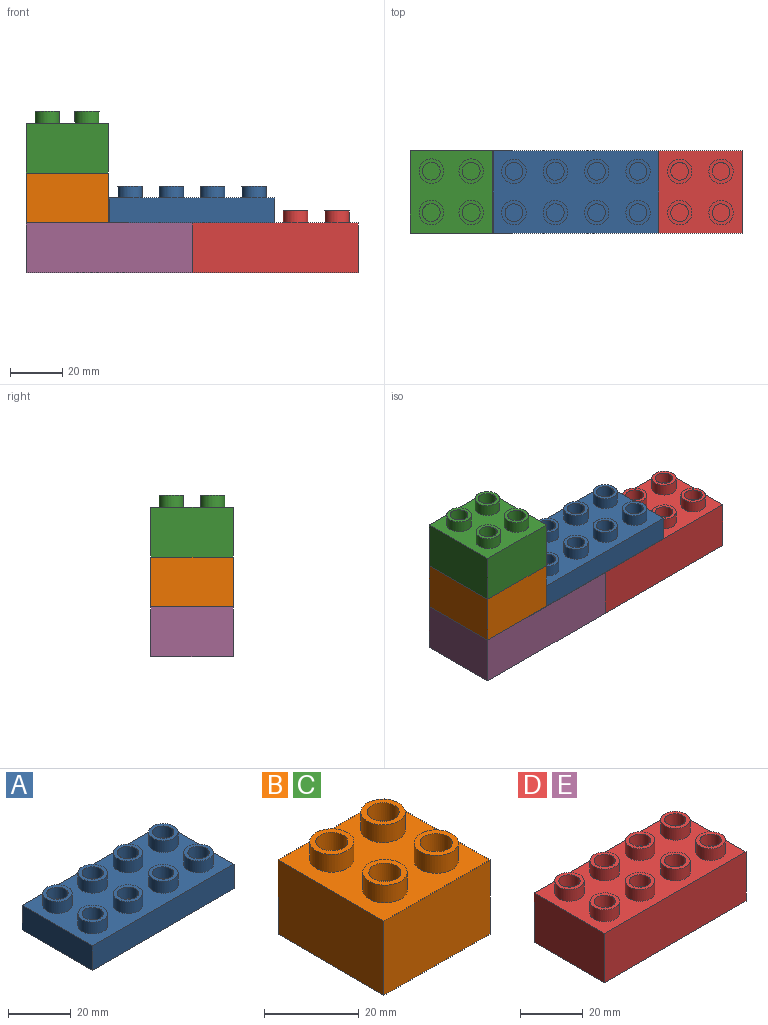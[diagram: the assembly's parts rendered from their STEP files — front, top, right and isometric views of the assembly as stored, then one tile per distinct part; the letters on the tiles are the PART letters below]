
ASSEMBLY  parts=5 mates=4
PART A: 38 faces, bbox 63.8x31.7x14.2 mm
  f0: plane 31.7x9.6mm, normal (-1,0,0), area 304.3mm2, adj f1,f3,f4,f5
  f1: plane 63.8x9.6mm, normal (0,-1,0), area 612.5mm2, adj f0,f2,f4,f5
  f2: plane 31.7x9.6mm, normal (1,0,0), area 304.3mm2, adj f1,f3,f4,f5
  f3: plane 63.8x9.6mm, normal (0,1,0), area 612.5mm2, adj f0,f2,f4,f5
  f4: plane 63.8x31.7mm, normal (0,0,1), area 1467.3mm2, adj f0,f1,f2,f3,f7,f11,f15,f19
  f5: plane 63.8x31.7mm, normal (0,0,-1), area 2022.5mm2, adj f0,f1,f2,f3
  f6: cylinder r=3.4mm len=6.8mm, axis (0,0,-1), area 98.3mm2, adj f8,f9
  f7: cylinder r=4.7mm len=9.4mm, axis (0,0,-1), area 135.8mm2, adj f4,f8
  f8: plane 9.4x9.4mm, normal (0,0,1), area 33.1mm2, adj f6,f7
  f9: plane 6.8x6.8mm, normal (0,0,1), area 36.3mm2, adj f6
  f10: cylinder r=3.4mm len=6.8mm, axis (0,0,-1), area 98.3mm2, adj f12,f13
  f11: cylinder r=4.7mm len=9.4mm, axis (0,0,-1), area 135.8mm2, adj f4,f12
  f12: plane 9.4x9.4mm, normal (0,0,1), area 33.1mm2, adj f10,f11
  f13: plane 6.8x6.8mm, normal (0,0,1), area 36.3mm2, adj f10
  f14: cylinder r=3.4mm len=6.8mm, axis (0,0,-1), area 98.3mm2, adj f16,f17
  f15: cylinder r=4.7mm len=9.4mm, axis (0,0,-1), area 135.8mm2, adj f4,f16
  f16: plane 9.4x9.4mm, normal (0,0,1), area 33.1mm2, adj f14,f15
  f17: plane 6.8x6.8mm, normal (0,0,1), area 36.3mm2, adj f14
  f18: cylinder r=3.4mm len=6.8mm, axis (0,0,-1), area 98.3mm2, adj f20,f21
  f19: cylinder r=4.7mm len=9.4mm, axis (0,0,-1), area 135.8mm2, adj f4,f20
  f20: plane 9.4x9.4mm, normal (0,0,1), area 33.1mm2, adj f18,f19
  f21: plane 6.8x6.8mm, normal (0,0,1), area 36.3mm2, adj f18
  f22: cylinder r=4.7mm len=9.4mm, axis (0,0,-1), area 135.8mm2, adj f4,f24
  f23: cylinder r=3.4mm len=6.8mm, axis (0,0,-1), area 98.3mm2, adj f24,f25
  f24: plane 9.4x9.4mm, normal (0,0,1), area 33.1mm2, adj f22,f23
  f25: plane 6.8x6.8mm, normal (0,0,1), area 36.3mm2, adj f23
  f26: cylinder r=4.7mm len=9.4mm, axis (0,0,-1), area 135.8mm2, adj f4,f28
  f27: cylinder r=3.4mm len=6.8mm, axis (0,0,-1), area 98.3mm2, adj f28,f29
  f28: plane 9.4x9.4mm, normal (0,0,1), area 33.1mm2, adj f26,f27
  f29: plane 6.8x6.8mm, normal (0,0,1), area 36.3mm2, adj f27
  f30: cylinder r=4.7mm len=9.4mm, axis (0,0,-1), area 135.8mm2, adj f4,f32
  f31: cylinder r=3.4mm len=6.8mm, axis (0,0,-1), area 98.3mm2, adj f32,f33
  f32: plane 9.4x9.4mm, normal (0,0,1), area 33.1mm2, adj f30,f31
  f33: plane 6.8x6.8mm, normal (0,0,1), area 36.3mm2, adj f31
  f34: cylinder r=4.7mm len=9.4mm, axis (0,0,-1), area 135.8mm2, adj f4,f36
  f35: cylinder r=3.4mm len=6.8mm, axis (0,0,-1), area 98.3mm2, adj f36,f37
  f36: plane 9.4x9.4mm, normal (0,0,1), area 33.1mm2, adj f34,f35
  f37: plane 6.8x6.8mm, normal (0,0,1), area 36.3mm2, adj f35
PART B: 22 faces, bbox 31.7x31.7x23.8 mm
  f0: plane 31.7x19.2mm, normal (-1,0,0), area 608.6mm2, adj f1,f3,f4,f5
  f1: plane 31.7x19.2mm, normal (0,-1,0), area 608.6mm2, adj f0,f2,f4,f5
  f2: plane 31.7x19.2mm, normal (1,0,0), area 608.6mm2, adj f1,f3,f4,f5
  f3: plane 31.7x19.2mm, normal (0,1,0), area 608.6mm2, adj f0,f2,f4,f5
  f4: plane 31.7x31.7mm, normal (0,0,1), area 727.3mm2, adj f0,f1,f2,f3,f7,f10,f14,f19
  f5: plane 31.7x31.7mm, normal (0,0,-1), area 1004.9mm2, adj f0,f1,f2,f3
  f6: cylinder r=3.4mm len=6.8mm, axis (0,0,-1), area 98.3mm2, adj f8,f9
  f7: cylinder r=4.7mm len=9.4mm, axis (0,0,-1), area 135.8mm2, adj f4,f8
  f8: plane 9.4x9.4mm, normal (0,0,1), area 33.1mm2, adj f6,f7
  f9: plane 6.8x6.8mm, normal (0,0,1), area 36.3mm2, adj f6
  f10: cylinder r=4.7mm len=9.4mm, axis (0,0,-1), area 135.8mm2, adj f4,f12
  f11: cylinder r=3.4mm len=6.8mm, axis (0,0,-1), area 98.3mm2, adj f12,f13
  f12: plane 9.4x9.4mm, normal (0,0,1), area 33.1mm2, adj f10,f11
  f13: plane 6.8x6.8mm, normal (0,0,1), area 36.3mm2, adj f11
  f14: cylinder r=4.7mm len=9.4mm, axis (0,0,-1), area 135.8mm2, adj f4,f16
  f15: cylinder r=3.4mm len=6.8mm, axis (0,0,-1), area 98.3mm2, adj f16,f17
  f16: plane 9.4x9.4mm, normal (0,0,1), area 33.1mm2, adj f14,f15
  f17: plane 6.8x6.8mm, normal (0,0,1), area 36.3mm2, adj f15
  f18: cylinder r=3.4mm len=6.8mm, axis (0,0,-1), area 98.3mm2, adj f20,f21
  f19: cylinder r=4.7mm len=9.4mm, axis (0,0,-1), area 135.8mm2, adj f4,f20
  f20: plane 9.4x9.4mm, normal (0,0,1), area 33.1mm2, adj f18,f19
  f21: plane 6.8x6.8mm, normal (0,0,1), area 36.3mm2, adj f18
PART C: same geometry as B
PART D: 38 faces, bbox 63.8x31.7x23.8 mm
  f0: plane 31.7x19.2mm, normal (-1,0,0), area 608.6mm2, adj f1,f3,f4,f5
  f1: plane 63.8x19.2mm, normal (0,-1,0), area 1225mm2, adj f0,f2,f4,f5
  f2: plane 31.7x19.2mm, normal (1,0,0), area 608.6mm2, adj f1,f3,f4,f5
  f3: plane 63.8x19.2mm, normal (0,1,0), area 1225mm2, adj f0,f2,f4,f5
  f4: plane 63.8x31.7mm, normal (0,0,1), area 1467.3mm2, adj f0,f1,f2,f3,f7,f11,f15,f19
  f5: plane 63.8x31.7mm, normal (0,0,-1), area 2022.5mm2, adj f0,f1,f2,f3
  f6: cylinder r=3.4mm len=6.8mm, axis (0,0,-1), area 98.3mm2, adj f8,f9
  f7: cylinder r=4.7mm len=9.4mm, axis (0,0,-1), area 135.8mm2, adj f4,f8
  f8: plane 9.4x9.4mm, normal (0,0,1), area 33.1mm2, adj f6,f7
  f9: plane 6.8x6.8mm, normal (0,0,1), area 36.3mm2, adj f6
  f10: cylinder r=3.4mm len=6.8mm, axis (0,0,-1), area 98.3mm2, adj f12,f13
  f11: cylinder r=4.7mm len=9.4mm, axis (0,0,-1), area 135.8mm2, adj f4,f12
  f12: plane 9.4x9.4mm, normal (0,0,1), area 33.1mm2, adj f10,f11
  f13: plane 6.8x6.8mm, normal (0,0,1), area 36.3mm2, adj f10
  f14: cylinder r=3.4mm len=6.8mm, axis (0,0,-1), area 98.3mm2, adj f16,f17
  f15: cylinder r=4.7mm len=9.4mm, axis (0,0,-1), area 135.8mm2, adj f4,f16
  f16: plane 9.4x9.4mm, normal (0,0,1), area 33.1mm2, adj f14,f15
  f17: plane 6.8x6.8mm, normal (0,0,1), area 36.3mm2, adj f14
  f18: cylinder r=3.4mm len=6.8mm, axis (0,0,-1), area 98.3mm2, adj f20,f21
  f19: cylinder r=4.7mm len=9.4mm, axis (0,0,-1), area 135.8mm2, adj f4,f20
  f20: plane 9.4x9.4mm, normal (0,0,1), area 33.1mm2, adj f18,f19
  f21: plane 6.8x6.8mm, normal (0,0,1), area 36.3mm2, adj f18
  f22: cylinder r=4.7mm len=9.4mm, axis (0,0,-1), area 135.8mm2, adj f4,f24
  f23: cylinder r=3.4mm len=6.8mm, axis (0,0,-1), area 98.3mm2, adj f24,f25
  f24: plane 9.4x9.4mm, normal (0,0,1), area 33.1mm2, adj f22,f23
  f25: plane 6.8x6.8mm, normal (0,0,1), area 36.3mm2, adj f23
  f26: cylinder r=4.7mm len=9.4mm, axis (0,0,-1), area 135.8mm2, adj f4,f28
  f27: cylinder r=3.4mm len=6.8mm, axis (0,0,-1), area 98.3mm2, adj f28,f29
  f28: plane 9.4x9.4mm, normal (0,0,1), area 33.1mm2, adj f26,f27
  f29: plane 6.8x6.8mm, normal (0,0,1), area 36.3mm2, adj f27
  f30: cylinder r=4.7mm len=9.4mm, axis (0,0,-1), area 135.8mm2, adj f4,f32
  f31: cylinder r=3.4mm len=6.8mm, axis (0,0,-1), area 98.3mm2, adj f32,f33
  f32: plane 9.4x9.4mm, normal (0,0,1), area 33.1mm2, adj f30,f31
  f33: plane 6.8x6.8mm, normal (0,0,1), area 36.3mm2, adj f31
  f34: cylinder r=4.7mm len=9.4mm, axis (0,0,-1), area 135.8mm2, adj f4,f36
  f35: cylinder r=3.4mm len=6.8mm, axis (0,0,-1), area 98.3mm2, adj f36,f37
  f36: plane 9.4x9.4mm, normal (0,0,1), area 33.1mm2, adj f34,f35
  f37: plane 6.8x6.8mm, normal (0,0,1), area 36.3mm2, adj f35
PART E: same geometry as D
PLACE A t=(0,0,19.2)mm
PLACE B t=(-47.95,0,19.2)mm
PLACE C t=(-47.95,0,38.4)mm
PLACE D t=(31.9,0,0)mm
PLACE E t=(-31.9,0,0)mm
MATE fastened B.f5 <-> E.f4  axis (0,0,-1) through (-63.8,0,19.2)mm
MATE fastened A.f5 <-> D.f4  axis (0,0,-1) through (0,0,19.2)mm
MATE fastened E.f2 <-> D.f0  axis (1,0,0) through (0,0,9.6)mm
MATE fastened B.f4 <-> C.f5  axis (0,0,1) through (-63.8,0,38.4)mm
